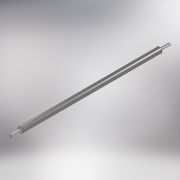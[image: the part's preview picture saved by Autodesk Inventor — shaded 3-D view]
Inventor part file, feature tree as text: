
AUTODESK INVENTOR PART (.ipt)
format: ipt  version: 2022 (Build 260153000, 153)  size: 123,392 bytes
history: native  units: mm
features: other x2, thread x1, sketch x1
ambient origin geometry x8: Origin, YZ Plane, XZ Plane, XY Plane, X Axis, Y Axis, Z Axis, Center Point
bodies: Body1 (feature_tree)
feature tree (4):
  other  "Sólido1"
  other  "Revolução1"
  thread  "Rosca1"  [1 undecoded]
  sketch  "Esboço1"  dims[d1=25.0mm d2=4.0mm d3=350.0mm d4=4.0mm d5=25.0mm d6=90.0deg d7=350.0mm d8=0.0mm]
note: 1 required parameter value undecoded (feature->parameter linkage not recoverable at this tier; creation-order binding heuristic only, values carry confidence <= 0.55)
